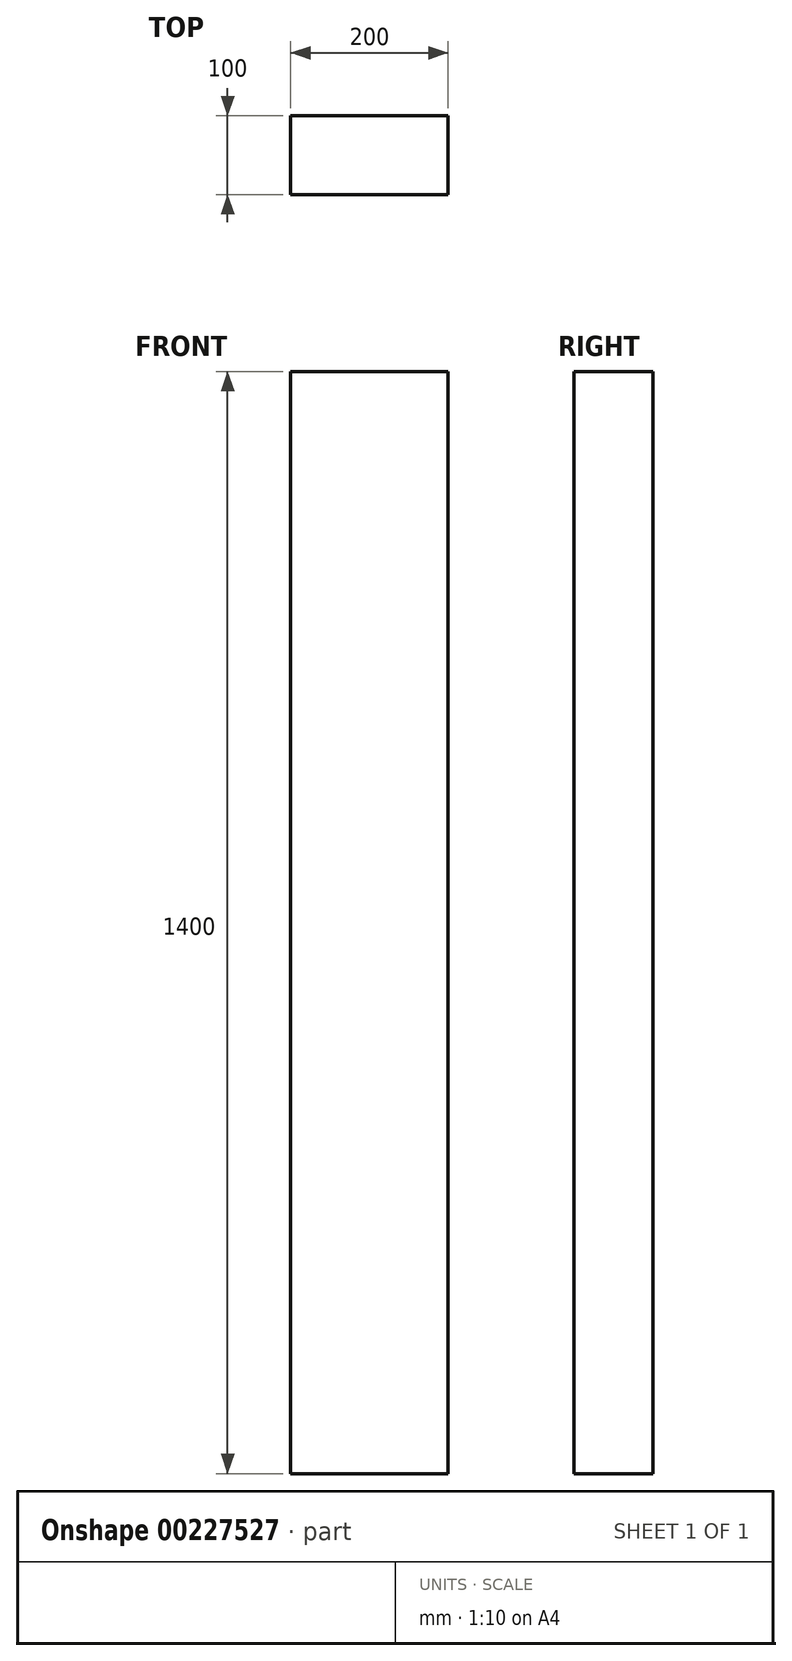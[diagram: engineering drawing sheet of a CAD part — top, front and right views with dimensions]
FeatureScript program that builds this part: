
annotation { "Feature Type Name" : "Feature", "Feature Type Description" : "" }
export const myFeature = defineFeature(function(context is Context, id is Id, definition is map)
    precondition{}
    {
        {
            var Q0;
            Q0=qCreatedBy(makeId("Front.planeOp"),FACE);
            var sketch = newSketch(context, id + "F0", { "sketchPlane" : qUnion([Q0])});
            skLineSegment(sketch, "E0.bottom", {"start": v(-100, 700) * mm, "end": v(100, 700) * mm});
            skLineSegment(sketch, "E0.top", {"start": v(-100, -700) * mm, "end": v(100, -700) * mm});
            skLineSegment(sketch, "E0.left", {"start": v(-100, 700) * mm, "end": v(-100, -700) * mm});
            skLineSegment(sketch, "E0.right", {"start": v(100, 700) * mm, "end": v(100, -700) * mm});
            skPoint(sketch, "E0.middle", {"position": v(0, 0) * mm});
            skLineSegment(sketch, "E1", {"start": v(0, 0) * mm, "end": v(0, 600) * mm});
            skPoint(sketch, "E2.middle", {"position": v(0, 600) * mm});
            skSolve(sketch);
        }
        {
            var Q0;
            Q0 = qSketchRegion(id + "F0", true);
            extrude(context, id + "F1", {"entities" : qUnion([Q0]), "oppositeDirection" : true, "depth" : 100 * mm});
        }
    });
